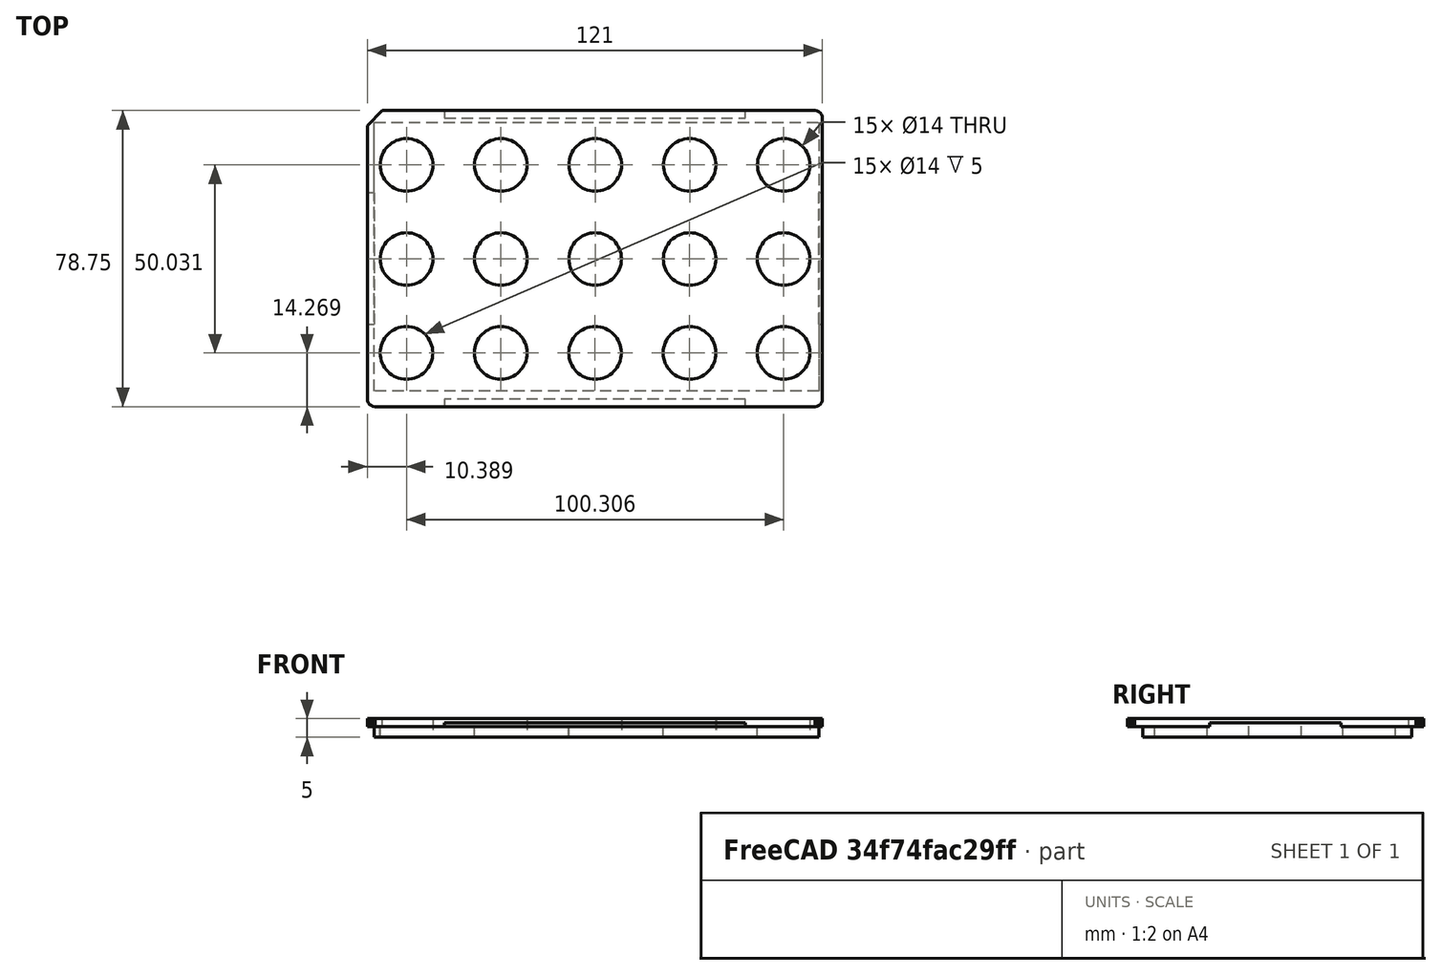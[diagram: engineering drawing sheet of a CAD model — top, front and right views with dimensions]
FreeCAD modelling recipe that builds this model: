
FCSTD DOCUMENT  (FreeCAD 0.21R33694 (Git))
Label: 5ml_top_part
License: All rights reserved
LicenseURL: http://en.wikipedia.org/wiki/All_rights_reserved
objects: Part::Feature×2, Part::Refine×2, PartDesign::FeatureBase×2, PartDesign::Body×2, Mesh::Feature×1, Part::Box×1, Part::Cut×1, Sketcher::SketchObject×1, PartDesign::Pad×1
note: 13 computed .brp shape members not serialized (recipe doc carries the construction recipe); baked Part::Feature solids carry a one-line shape summary decoded from their .brp

FEATURE [Mesh::Feature] Opentrons_15mL_Tube_Rack_Top
FEATURE [Part::Feature] Opentrons_15mL_Tube_Rack_Top001
  shape: bbox 121 x 78.75 x 10 mm, 1658 faces, 0 solids (baked)
FEATURE [Part::Refine] Opentrons_15mL_Tube_Rack_Top002
  Source = -> Opentrons_15mL_Tube_Rack_Top001
FEATURE [Part::Feature] Opentrons_15mL_Tube_Rack_Top002_solid  label="Solide_importé"
  shape: bbox 121 x 78.75 x 10 mm, 401 faces (baked)
FEATURE [PartDesign::FeatureBase] BaseFeature
  BaseFeature = -> Opentrons_15mL_Tube_Rack_Top002_solid
FEATURE [PartDesign::Body] Body
  BaseFeature = -> Opentrons_15mL_Tube_Rack_Top002_solid
  Group = -> [BaseFeature]
  Origin = -> Origin
  Tip = -> BaseFeature
FEATURE [Part::Box] Box  label="Cube"
  AttacherType = Attacher::AttachEngine3D
  Height = 10
  Length = 140
  Placement = pos=(-11.7,-4.8,2.2) rot=(0,0,1;0rad)
  Width = 90
FEATURE [Part::Cut] Cut
  Base = -> Body
  Tool = -> Box
FEATURE [PartDesign::FeatureBase] BaseFeature001
  BaseFeature = -> Cut
FEATURE [Sketcher::SketchObject] Sketch
  FullyConstrained = false
  MapMode = 5
  Placement = pos=(0,0,2.2) rot=(0,0,1;0rad)
  Support = -> [BaseFeature001]
  sketch-geometry (19):
    g0: Circle CenterX=35.5 CenterY=64.3 CenterZ=0 NormalX=0 NormalY=0 NormalZ=1 AngleXU=0 Radius=7
    g1: Circle CenterX=60.5779 CenterY=64.3 CenterZ=0 NormalX=0 NormalY=0 NormalZ=1 AngleXU=0 Radius=7
    g2: Circle CenterX=85.6948 CenterY=64.3 CenterZ=0 NormalX=0 NormalY=0 NormalZ=1 AngleXU=0 Radius=7
    g3: Circle CenterX=110.695 CenterY=64.3 CenterZ=0 NormalX=0 NormalY=0 NormalZ=1 AngleXU=0 Radius=7
    g4: Circle CenterX=10.4267 CenterY=64.3 CenterZ=0 NormalX=0 NormalY=0 NormalZ=1 AngleXU=0 Radius=7
    g5: Circle CenterX=35.4959 CenterY=39.2605 CenterZ=0 NormalX=0 NormalY=0 NormalZ=1 AngleXU=0 Radius=7
    g6: Circle CenterX=60.5738 CenterY=39.2605 CenterZ=0 NormalX=0 NormalY=0 NormalZ=1 AngleXU=0 Radius=7
    g7: Circle CenterX=85.6907 CenterY=39.2605 CenterZ=0 NormalX=0 NormalY=0 NormalZ=1 AngleXU=0 Radius=7
    g8: Circle CenterX=110.691 CenterY=39.2605 CenterZ=0 NormalX=0 NormalY=0 NormalZ=1 AngleXU=0 Radius=7
    g9: Circle CenterX=10.4226 CenterY=39.2605 CenterZ=0 NormalX=0 NormalY=0 NormalZ=1 AngleXU=0 Radius=7
    g10: Circle CenterX=35.4625 CenterY=14.2686 CenterZ=0 NormalX=0 NormalY=0 NormalZ=1 AngleXU=0 Radius=7
    g11: Circle CenterX=60.5403 CenterY=14.2686 CenterZ=0 NormalX=0 NormalY=0 NormalZ=1 AngleXU=0 Radius=7
    g12: Circle CenterX=85.6572 CenterY=14.2686 CenterZ=0 NormalX=0 NormalY=0 NormalZ=1 AngleXU=0 Radius=7
    g13: Circle CenterX=110.657 CenterY=14.2686 CenterZ=0 NormalX=0 NormalY=0 NormalZ=1 AngleXU=0 Radius=7
    g14: Circle CenterX=10.3891 CenterY=14.2686 CenterZ=0 NormalX=0 NormalY=0 NormalZ=1 AngleXU=0 Radius=7
    g15: LineSegment StartX=1.84748 StartY=75.6671 StartZ=0 EndX=120.043 EndY=75.6671 EndZ=0
    g16: LineSegment StartX=120.043 StartY=75.6671 StartZ=0 EndX=120.043 EndY=4.13362 EndZ=0
    g17: LineSegment StartX=120.043 StartY=4.13362 StartZ=0 EndX=1.84748 EndY=4.13362 EndZ=0
    g18: LineSegment StartX=1.84748 StartY=4.13362 StartZ=0 EndX=1.84748 EndY=75.6671 EndZ=0
  constraints (28):
    c: DistanceX(g2,g3) = 25
    c: Horizontal(g0,g1)
    c: Horizontal(g1,g2)
    c: Horizontal(g2,g3)
    c: Horizontal(g4,g0)
    c: DistanceY(g-1,g4) = 64.3
    c: DistanceX(g7,g8) = 25
    c: Horizontal(g5,g6)
    c: Horizontal(g6,g7)
    c: Horizontal(g7,g8)
    c: Horizontal(g9,g5)
    c: DistanceX(g12,g13) = 25
    c: Horizontal(g10,g11)
    c: Horizontal(g11,g12)
    c: Horizontal(g12,g13)
    c: Horizontal(g14,g10)
    c: Equal(g4, g0-g3) x4
    c: Diameter(g4) = 14
    c: Equal(g5, g6-g14) x9
    c: Diameter(g5) = 14
    c: Coincident(g15,g16)
    c: Coincident(g16,g17)
    c: Coincident(g17,g18)
    c: Coincident(g18,g15)
    c: Horizontal(g15)
    c: Horizontal(g17)
    c: Vertical(g16)
    c: Vertical(g18)
FEATURE [PartDesign::Pad] Pad
  BaseFeature = -> BaseFeature001
  Direction = (0,0,1)
  Length = 5
  Length2 = 10
  Profile = -> Sketch
  ReferenceAxis = -> Sketch [N_Axis]
  Reversed = true
  Type = 0
FEATURE [PartDesign::Body] Body001
  BaseFeature = -> Cut
  Group = -> [BaseFeature001,Sketch,Pad]
  Origin = -> Origin001
  Tip = -> Pad
FEATURE [Part::Refine] Pad001
  Source = -> Pad
